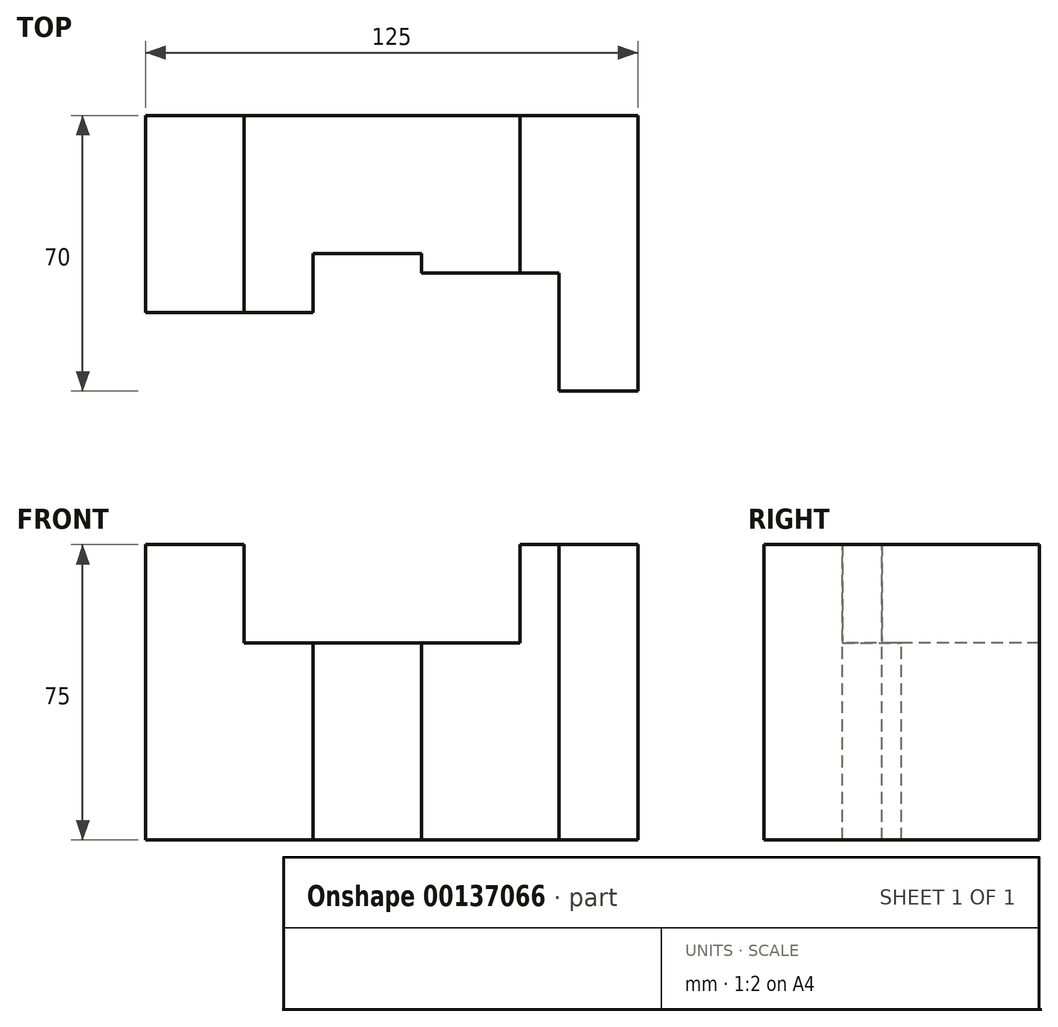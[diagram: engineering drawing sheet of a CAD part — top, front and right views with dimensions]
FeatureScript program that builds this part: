
annotation { "Feature Type Name" : "Feature", "Feature Type Description" : "" }
export const myFeature = defineFeature(function(context is Context, id is Id, definition is map)
    precondition{}
    {
        {
            var Q0;
            Q0=qCreatedBy(makeId("Front.planeOp"),FACE);
            var sketch = newSketch(context, id + "F0", { "sketchPlane" : qUnion([Q0])});
            skLineSegment(sketch, "E0", {"start": v(0, 0) * mm, "end": v(0, 75) * mm});
            skLineSegment(sketch, "E1", {"start": v(0, 75) * mm, "end": v(125, 75) * mm});
            skLineSegment(sketch, "E2", {"start": v(125, 75) * mm, "end": v(125, 0) * mm});
            skLineSegment(sketch, "E3", {"start": v(125, 0) * mm, "end": v(0, 0) * mm});
            skSolve(sketch);
        }
        {
            var Q0;
            Q0 = qSketchRegion(id + "F0", true);
            extrude(context, id + "F1", {"entities" : qUnion([Q0]), "oppositeDirection" : true, "depth" : 70 * mm});
        }
        {
            var Q0;
            Q0=makeQuery(id+"F1.opExtrude","CAP_FACE",FACE,{"disambiguationData":[OSD([sQuery(id+"F0.wireOp",EDGE,"E0"),sQuery(id+"F0.wireOp",EDGE,"E1"),sQuery(id+"F0.wireOp",EDGE,"E2"),sQuery(id+"F0.wireOp",EDGE,"E3")])],"isStart":true});
            var sketch = newSketch(context, id + "F2", { "sketchPlane" : qUnion([Q0])});
            skLineSegment(sketch, "E4.bottom", {"start": v(25, 75) * mm, "end": v(95, 75) * mm});
            skLineSegment(sketch, "E4.top", {"start": v(25, 50) * mm, "end": v(95, 50) * mm});
            skLineSegment(sketch, "E4.left", {"start": v(25, 75) * mm, "end": v(25, 50) * mm});
            skLineSegment(sketch, "E4.right", {"start": v(95, 75) * mm, "end": v(95, 50) * mm});
            skSolve(sketch);
        }
        {
            var Q0;
            Q0 = qSketchRegion(id + "F2", true);
            extrude(context, id + "F3", {"entities" : qUnion([Q0]), "operationType" : NewBodyOperationType.REMOVE, "endBound" : BoundingType.THROUGH_ALL, "oppositeDirection" : true, "depth" : 25 * mm});
        }
        {
            var Q0;
            {var subQ1=sQuery(id+"F0.wireOp",EDGE,"E2");var subQ2=sQuery(id+"F0.wireOp",EDGE,"E1");Q0=makeQuery(id+"F3.boolean.opBoolean","SPLIT",FACE,{"disambiguationData":[TD([makeQuery(id+"F1.opExtrude","SWEPT_FACE",FACE,{"disambiguationData":[OSD([subQ1])]})])],"derivedFrom":makeQuery(id+"F1.opExtrude","SWEPT_FACE",FACE,{"disambiguationData":[OSD([subQ2])]})});}
            var sketch = newSketch(context, id + "F4", { "sketchPlane" : qUnion([Q0])});
            skLineSegment(sketch, "E5", {"start": v(105, 0) * mm, "end": v(105, 30) * mm});
            skLineSegment(sketch, "E6", {"start": v(105, 30) * mm, "end": v(70, 30) * mm});
            skLineSegment(sketch, "E7", {"start": v(70, 30) * mm, "end": v(70, 35) * mm});
            skLineSegment(sketch, "E8", {"start": v(70, 35) * mm, "end": v(42.5, 35) * mm});
            skLineSegment(sketch, "E9", {"start": v(42.5, 35) * mm, "end": v(42.5, 20) * mm});
            skLineSegment(sketch, "E10", {"start": v(42.5, 20) * mm, "end": v(0, 20) * mm});
            skLineSegment(sketch, "E11", {"start": v(0, 20) * mm, "end": v(0, 0) * mm});
            skLineSegment(sketch, "E12", {"start": v(0, 0) * mm, "end": v(105, 0) * mm});
            skSolve(sketch);
        }
        {
            var Q0;
            Q0 = qSketchRegion(id + "F4", true);
            extrude(context, id + "F5", {"entities" : qUnion([Q0]), "operationType" : NewBodyOperationType.REMOVE, "endBound" : BoundingType.THROUGH_ALL, "oppositeDirection" : true, "depth" : 25 * mm});
        }
    });
